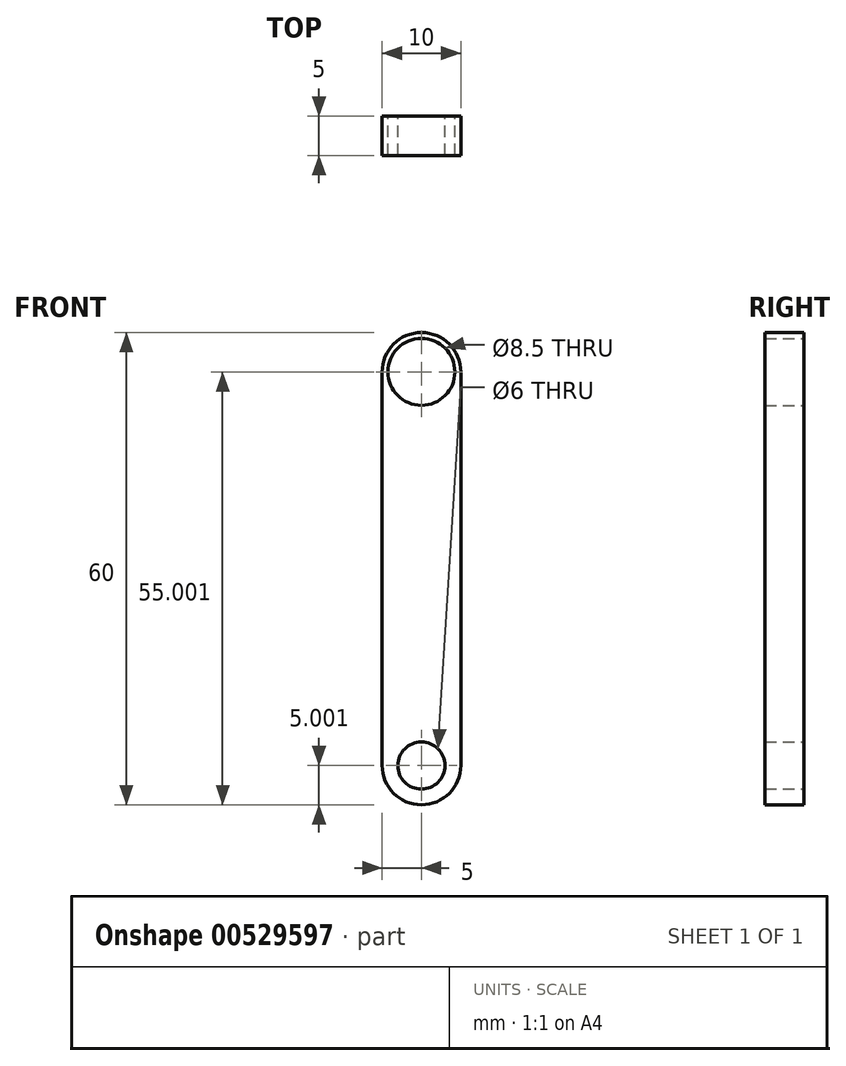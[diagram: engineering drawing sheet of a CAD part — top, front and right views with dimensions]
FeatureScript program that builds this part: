
annotation { "Feature Type Name" : "Feature", "Feature Type Description" : "" }
export const myFeature = defineFeature(function(context is Context, id is Id, definition is map)
    precondition{}
    {
        {
            var Q0;
            Q0=qCreatedBy(makeId("Front.planeOp"),FACE);
            var sketch = newSketch(context, id + "F0", { "sketchPlane" : qUnion([Q0])});
            skArc(sketch, "E0", {"start": v(5, 39.83) * mm, "mid": v(0, 44.83) * mm, "end": v(-5, 39.83) * mm});
            skArc(sketch, "E1", {"start": v(-5, -10.17) * mm, "mid": v(0, -15.17) * mm, "end": v(5, -10.17) * mm});
            skCircle(sketch, "E2", {"center": v(0, 39.83) * mm, "radius": 4.25 * mm});
            skCircle(sketch, "E3", {"center": v(0, -10.17) * mm, "radius": 3 * mm});
            skLineSegment(sketch, "E4", {"start": v(5, 39.83) * mm, "end": v(5, -10.17) * mm});
            skLineSegment(sketch, "E5", {"start": v(-5, -10.17) * mm, "end": v(-5, 39.83) * mm});
            skSolve(sketch);
        }
        {
            var Q0;
            Q0 = qSketchRegion(id + "F0", true);
            extrude(context, id + "F1", {"entities" : qUnion([Q0]), "endBound" : BoundingType.SYMMETRIC, "depth" : 5 * mm, "offsetDistance" : 25 * mm});
        }
    });
